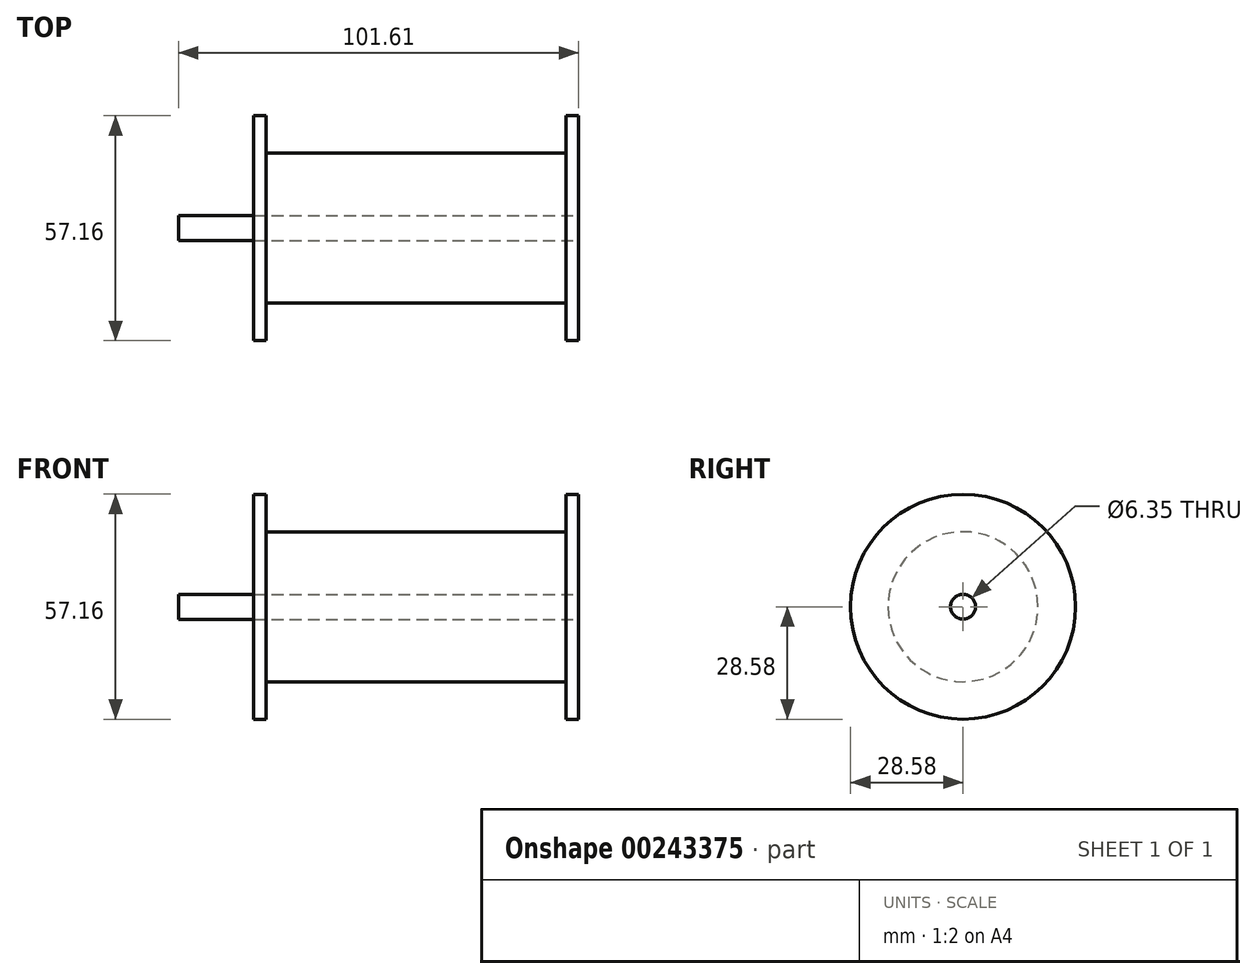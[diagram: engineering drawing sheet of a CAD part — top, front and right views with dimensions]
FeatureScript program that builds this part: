
annotation { "Feature Type Name" : "Feature", "Feature Type Description" : "" }
export const myFeature = defineFeature(function(context is Context, id is Id, definition is map)
    precondition{}
    {
        {
            var Q0;
            Q0=qCreatedBy(makeId("Right.planeOp"),FACE);
            var sketch = newSketch(context, id + "F0", { "sketchPlane" : qUnion([Q0])});
            skCircle(sketch, "E0", {"center": v(0, 0) * mm, "radius": 19.05 * mm});
            skSolve(sketch);
        }
        {
            var Q0;
            Q0 = qSketchRegion(id + "F0", true);
            extrude(context, id + "F1", {"entities" : qUnion([Q0]), "depth" : 38.1 * mm});
        }
        {
            var Q0;
            Q0=makeQuery(id+"F1.opExtrude","CAP_FACE",FACE,{"disambiguationData":[OSD([sQuery(id+"F0.wireOp",EDGE,"E0")])],"isStart":false});
            var sketch = newSketch(context, id + "F2", { "sketchPlane" : qUnion([Q0])});
            skCircle(sketch, "E1", {"center": v(0, 0) * mm, "radius": 28.57 * mm});
            skSolve(sketch);
        }
        {
            var Q0;
            Q0 = qSketchRegion(id + "F2", true);
            extrude(context, id + "F3", {"entities" : qUnion([Q0]), "operationType" : NewBodyOperationType.ADD, "depth" : 3.17 * mm});
        }
        {
            var Q0;
            Q0=makeQuery(id+"F1.opExtrude","SWEPT_BODY",BODY,{"disambiguationData":[OSD([sQuery(id+"F0.wireOp",EDGE,"E0")])]});
            var Q1;
            Q1=qCreatedBy(makeId("Right.planeOp"),FACE);
            mirror(context, id + "F4", {"operationType" : NewBodyOperationType.ADD, "entities" : qUnion([Q0]), "mirrorPlane" : qUnion([Q1])});
        }
        {
            var Q0;
            Q0=makeQuery(id+"F3.opExtrude","CAP_FACE",FACE,{"disambiguationData":[OSD([sQuery(id+"F2.wireOp",EDGE,"E1")])],"isStart":false});
            var sketch = newSketch(context, id + "F5", { "sketchPlane" : qUnion([Q0])});
            skCircle(sketch, "E2", {"center": v(0, 0) * mm, "radius": 3.18 * mm});
            skSolve(sketch);
        }
        {
            var Q0;
            Q0 = qSketchRegion(id + "F5", true);
            extrude(context, id + "F6", {"entities" : qUnion([Q0]), "oppositeDirection" : true, "depth" : 101.6 * mm});
        }
        {
            var Q0;
            Q0=makeQuery(id+"F6.opExtrude","SWEPT_BODY",BODY,{"disambiguationData":[OSD([sQuery(id+"F5.wireOp",EDGE,"E2")])]});
            var Q1;
            Q1=makeQuery(id+"F1.opExtrude","SWEPT_BODY",BODY,{"disambiguationData":[OSD([sQuery(id+"F0.wireOp",EDGE,"E0")])]});
            booleanBodies(context, id + "F7", {"operationType" : BooleanOperationType.SUBTRACTION, "tools" : qUnion([Q0]), "targets" : qUnion([Q1]), "keepTools" : true});
        }
    });
